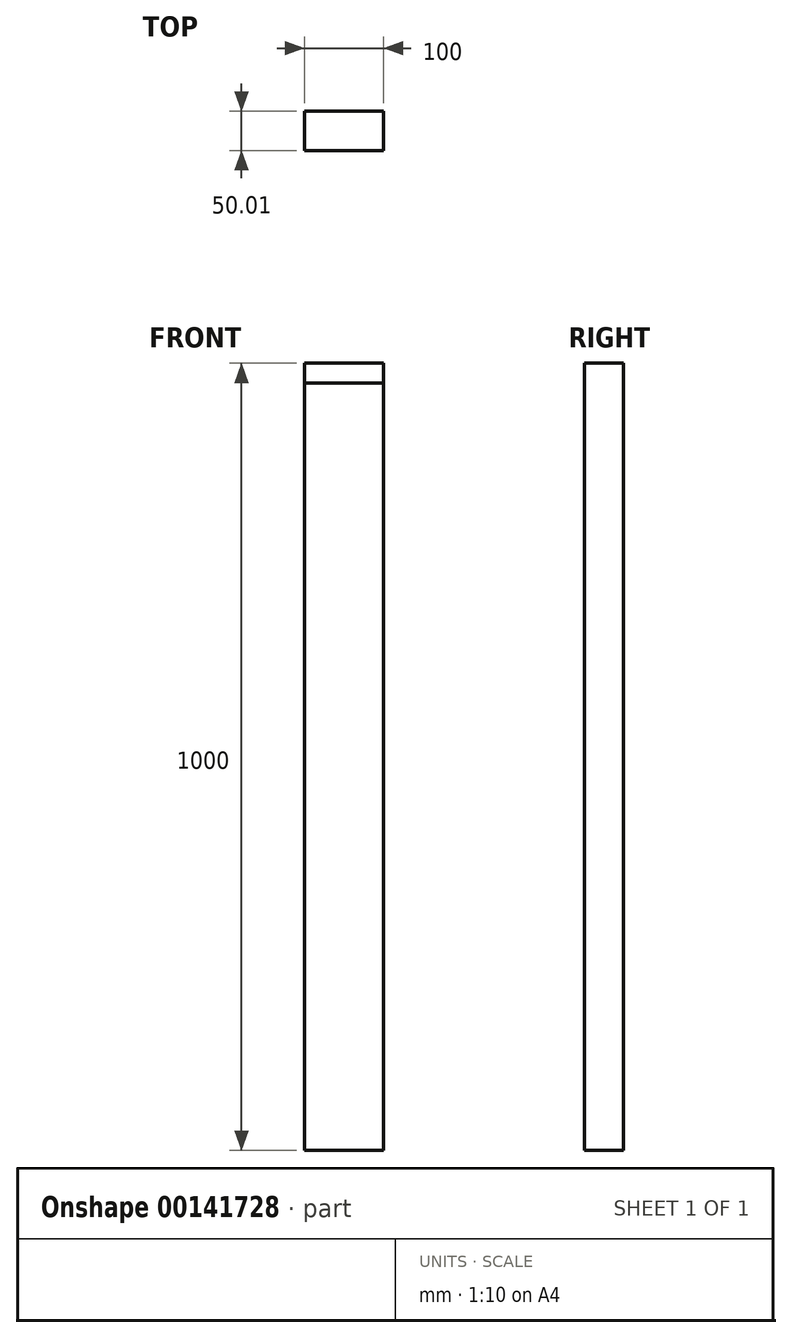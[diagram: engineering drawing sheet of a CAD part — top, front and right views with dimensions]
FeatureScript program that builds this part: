
annotation { "Feature Type Name" : "Feature", "Feature Type Description" : "" }
export const myFeature = defineFeature(function(context is Context, id is Id, definition is map)
    precondition{}
    {
        {
            var Q0;
            Q0=qCreatedBy(makeId("Top.planeOp"),FACE);
            var sketch = newSketch(context, id + "F0", { "sketchPlane" : qUnion([Q0])});
            skLineSegment(sketch, "E0.bottom", {"start": v(50, -25) * mm, "end": v(-50, -25) * mm});
            skLineSegment(sketch, "E0.top", {"start": v(50, 25) * mm, "end": v(-50, 25) * mm});
            skLineSegment(sketch, "E0.left", {"start": v(50, -25) * mm, "end": v(50, 25) * mm});
            skLineSegment(sketch, "E0.right", {"start": v(-50, -25) * mm, "end": v(-50, 25) * mm});
            skPoint(sketch, "E0.middle", {"position": v(0, 0) * mm});
            skSolve(sketch);
        }
        {
            var Q0;
            Q0=makeQuery(id+"F0.imprint","IMPRINT",FACE,{"disambiguationData":[TD([[makeQuery(id+"F0.imprint","IMPRINT",EDGE,{"derivedFrom":sQuery(id+"F0.wireOp",EDGE,"E0.bottom")}),-1.0]])]});
            extrude(context, id + "F1", {"entities" : qUnion([Q0]), "depth" : 1000 * mm});
        }
        {
            var Q0;
            Q0=makeQuery(id+"F1.opExtrude","SWEPT_FACE",FACE,{"disambiguationData":[OSD([sQuery(id+"F0.wireOp",EDGE,"E0.bottom")])]});
            var sketch = newSketch(context, id + "F2", { "sketchPlane" : qUnion([Q0])});
            skLineSegment(sketch, "E1", {"start": v(-50, 975) * mm, "end": v(50, 975) * mm});
            skLineSegment(sketch, "E2", {"start": v(-50, 975) * mm, "end": v(-50, 1000) * mm});
            skLineSegment(sketch, "E3", {"start": v(-50, 1000) * mm, "end": v(50, 1000) * mm});
            skLineSegment(sketch, "E4", {"start": v(50, 1000) * mm, "end": v(50, 975) * mm});
            skSolve(sketch);
        }
        {
            var Q0;
            Q0=makeQuery(id+"F2.imprint","IMPRINT",FACE,{"disambiguationData":[TD([[makeQuery(id+"F2.imprint","IMPRINT",EDGE,{"derivedFrom":sQuery(id+"F2.wireOp",EDGE,"E1")}),1.0]])]});
            var Q1;
            Q1=sQuery(id+"F2.wireOp",EDGE,"E1");
            var Q2;
            Q2=sQuery(id+"F2.wireOp",EDGE,"E2");
            var Q3;
            Q3=sQuery(id+"F2.wireOp",EDGE,"E3");
            var Q4;
            Q4=sQuery(id+"F2.wireOp",EDGE,"E4");
            extrude(context, id + "F3", {"entities" : qUnion([Q0]), "operationType" : NewBodyOperationType.ADD, "surfaceEntities" : qUnion([Q1, Q2, Q3, Q4]), "depth" : 0.01 * mm});
        }
    });
